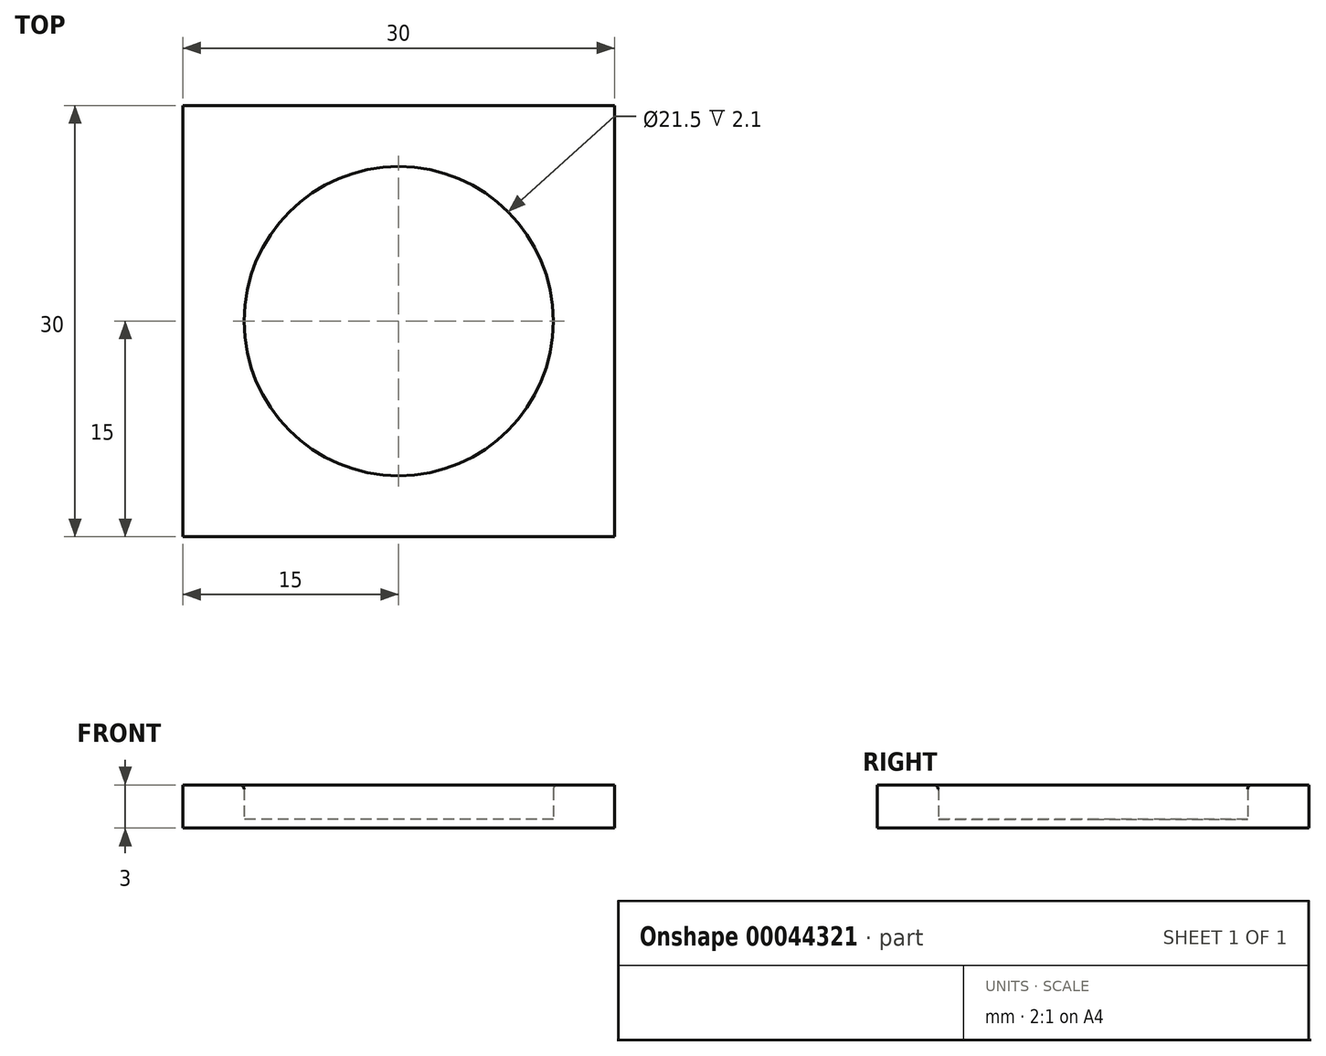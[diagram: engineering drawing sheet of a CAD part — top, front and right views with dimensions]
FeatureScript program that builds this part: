
annotation { "Feature Type Name" : "Feature", "Feature Type Description" : "" }
export const myFeature = defineFeature(function(context is Context, id is Id, definition is map)
    precondition{}
    {
        {
            var Q0;
            Q0=qCreatedBy(makeId("Top.planeOp"),FACE);
            var sketch = newSketch(context, id + "F0", { "sketchPlane" : qUnion([Q0])});
            skCircle(sketch, "E0", {"center": v(0, 0) * mm, "radius": 10.75 * mm});
            skLineSegment(sketch, "E1.bottom", {"start": v(15, -15) * mm, "end": v(-15, -15) * mm});
            skLineSegment(sketch, "E1.top", {"start": v(15, 15) * mm, "end": v(-15, 15) * mm});
            skLineSegment(sketch, "E1.left", {"start": v(15, -15) * mm, "end": v(15, 15) * mm});
            skLineSegment(sketch, "E1.right", {"start": v(-15, -15) * mm, "end": v(-15, 15) * mm});
            skSolve(sketch);
        }
        {
            var Q0;
            Q0=qSketchRegion(id+"F0",true);
            extrude(context, id + "F1", {"entities" : qUnion([Q0]), "depth" : 3 * mm});
        }
        {
            var Q0;
            Q0=makeQuery(id+"F0.imprint","IMPRINT",FACE,{"disambiguationData":[TD([[makeQuery(id+"F0.imprint","IMPRINT",EDGE,{"derivedFrom":sQuery(id+"F0.wireOp",EDGE,"E0")}),1.0]])]});
            extrude(context, id + "F2", {"entities" : qUnion([Q0]), "operationType" : NewBodyOperationType.ADD, "depth" : 0.6 * mm});
        }
        {
            var Q0;
            Q0=makeQuery(id+"F1.opExtrude","CAP_EDGE",EDGE,{"disambiguationData":[OSD([sQuery(id+"F0.wireOp",EDGE,"E0")])],"isStart":false});
            fillet(context, id + "F3", {"entities" : qUnion([Q0]), "radius" : 0.3 * mm, "tangentPropagation" : true, "allowEdgeOverflow" : false});
        }
    });
